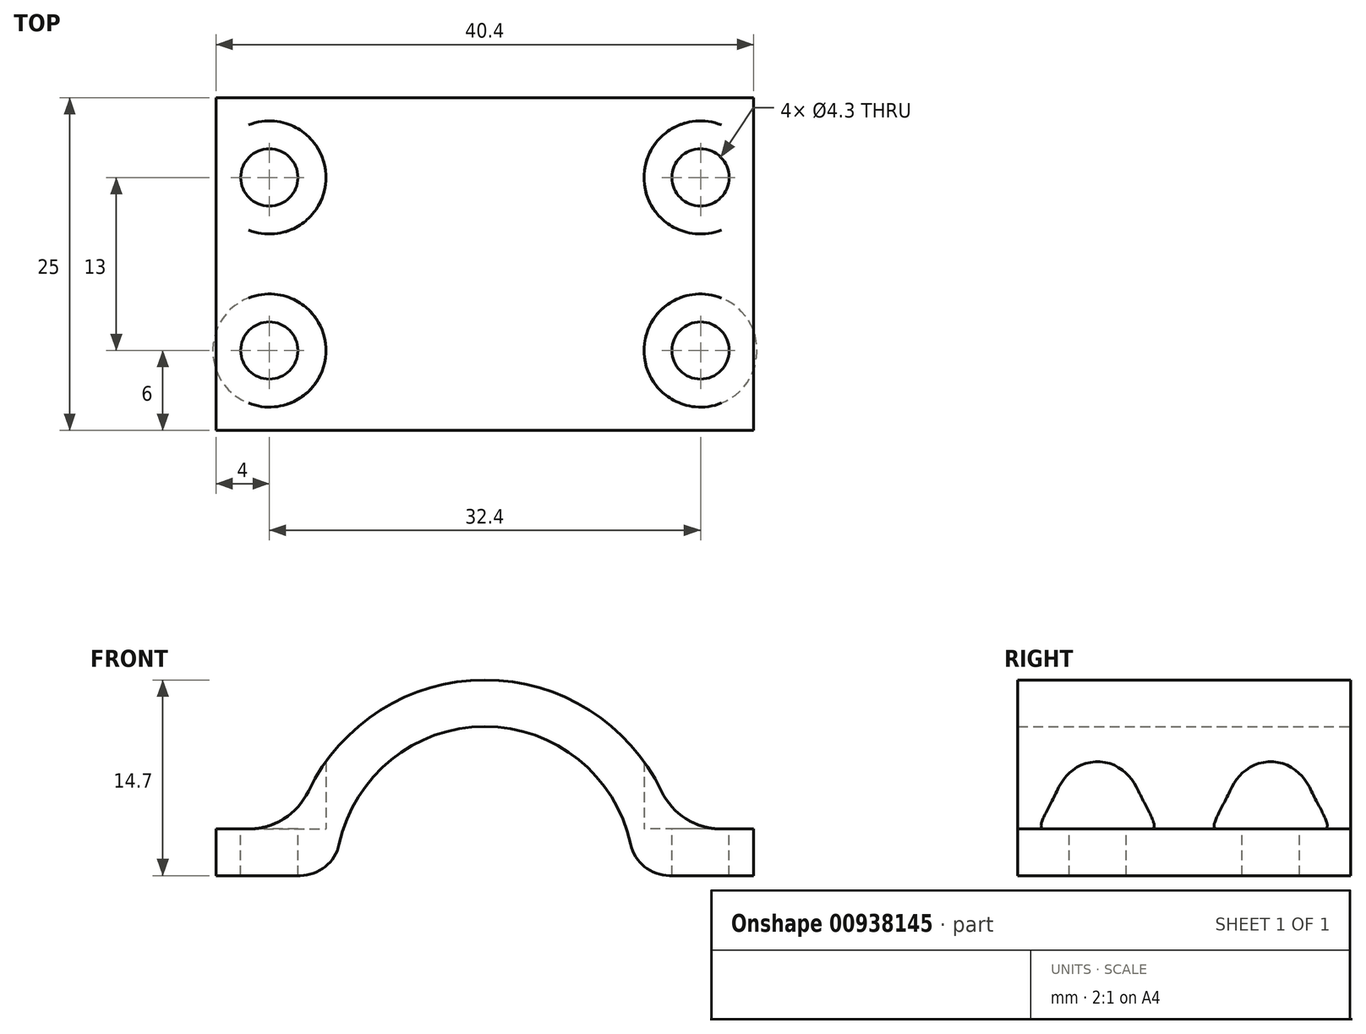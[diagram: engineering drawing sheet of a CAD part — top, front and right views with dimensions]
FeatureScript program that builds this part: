
annotation { "Feature Type Name" : "Feature", "Feature Type Description" : "" }
export const myFeature = defineFeature(function(context is Context, id is Id, definition is map)
    precondition{}
    {
        {
            var Q0;
            Q0=qCreatedBy(makeId("Front.planeOp"),FACE);
            var sketch = newSketch(context, id + "F0", { "sketchPlane" : qUnion([Q0])});
            skLineSegment(sketch, "E0", {"start": v(-13.88, 0) * mm, "end": v(-20.2, 0) * mm});
            skLineSegment(sketch, "E1", {"start": v(-20.2, 0) * mm, "end": v(-20.2, 3.5) * mm});
            skLineSegment(sketch, "E2", {"start": v(-20.2, 3.5) * mm, "end": v(-14.28, 3.5) * mm});
            skArc(sketch, "E3", {"start": v(-10.95, 2.37) * mm, "mid": v(0, 11.2) * mm, "end": v(10.95, 2.37) * mm});
            skArc(sketch, "E4", {"start": v(-14.28, 3.5) * mm, "mid": v(0, 14.7) * mm, "end": v(14.28, 3.5) * mm});
            skLineSegment(sketch, "E5", {"start": v(13.88, 0) * mm, "end": v(20.2, 0) * mm});
            skLineSegment(sketch, "E6", {"start": v(20.2, 0) * mm, "end": v(20.2, 3.5) * mm});
            skLineSegment(sketch, "E7", {"start": v(20.2, 3.5) * mm, "end": v(14.28, 3.5) * mm});
            skPoint(sketch, "E8.visualSharp", {"position": v(-11.2, 0) * mm});
            skArc(sketch, "E8.filletArc", {"start": v(-13.88, 0) * mm, "mid": v(-12, 0.67) * mm, "end": v(-10.95, 2.37) * mm});
            skPoint(sketch, "E9.visualSharp", {"position": v(11.2, 0) * mm});
            skArc(sketch, "E9.filletArc", {"start": v(10.95, 2.37) * mm, "mid": v(12, 0.67) * mm, "end": v(13.88, 0) * mm});
            skSolve(sketch);
        }
        {
            var Q0;
            Q0=makeQuery(id+"F0.imprint","IMPRINT",FACE,{"disambiguationData":[TD([[makeQuery(id+"F0.imprint","IMPRINT",EDGE,{"derivedFrom":sQuery(id+"F0.wireOp",EDGE,"E0")}),-1.0]])]});
            extrude(context, id + "F1", {"entities" : qUnion([Q0]), "depth" : 25 * mm, "offsetDistance" : 25 * mm});
        }
        {
            var Q0;
            Q0=makeQuery(id+"F1.opExtrude","SWEPT_FACE",FACE,{"disambiguationData":[OSD([sQuery(id+"F0.wireOp",EDGE,"E2")])]});
            var sketch = newSketch(context, id + "F2", { "sketchPlane" : qUnion([Q0])});
            skCircle(sketch, "E10", {"center": v(-16.2, -6) * mm, "radius": 2.15 * mm});
            skCircle(sketch, "E11", {"center": v(-16.2, -19) * mm, "radius": 2.15 * mm});
            skLineSegment(sketch, "E12", {"start": v(0, -12.5) * mm, "end": v(-26.72, -12.5) * mm, "construction": true});
            skCircle(sketch, "E13", {"center": v(16.2, -6) * mm, "radius": 2.15 * mm});
            skCircle(sketch, "E14", {"center": v(16.2, -19) * mm, "radius": 2.15 * mm});
            skCircle(sketch, "E15", {"center": v(-16.2, -6) * mm, "radius": 4.25 * mm});
            skCircle(sketch, "E16", {"center": v(16.2, -6) * mm, "radius": 4.25 * mm});
            skCircle(sketch, "E17", {"center": v(16.2, -19) * mm, "radius": 4.25 * mm});
            skCircle(sketch, "E18", {"center": v(-16.2, -19) * mm, "radius": 4.25 * mm});
            skSolve(sketch);
        }
        {
            var Q0;
            {var subQ0=sQuery(id+"F0.wireOp",EDGE,"E7");var subQ1=makeQuery(id+"F1.opExtrude","SWEPT_FACE",FACE,{"disambiguationData":[OSD([subQ0])]});var subQ2=sQuery(id+"F0.wireOp",EDGE,"E4");var subQ3=makeQuery(id+"F1.opExtrude","SWEPT_FACE",FACE,{"disambiguationData":[OSD([subQ2])]});var subQ4=sQuery(id+"F2.wireOp",EDGE,"E14");Q0=makeQuery(id+"F4.boolean.opBoolean","SPLIT",EDGE,{"disambiguationData":[topologyDisambiguationEdgeConnected([subQ3,subQ1]),TD([makeQuery(id+"F1.opExtrude","CAP_FACE",FACE,{"disambiguationData":[OSD([sQuery(id+"F0.wireOp",EDGE,"E0"),sQuery(id+"F0.wireOp",EDGE,"E1"),sQuery(id+"F0.wireOp",EDGE,"E2"),sQuery(id+"F0.wireOp",EDGE,"E3"),subQ2,sQuery(id+"F0.wireOp",EDGE,"E5"),sQuery(id+"F0.wireOp",EDGE,"E6"),subQ0,sQuery(id+"F0.wireOp",EDGE,"E8.filletArc"),sQuery(id+"F0.wireOp",EDGE,"E9.filletArc")])],"isStart":false}),subQ3,subQ1,makeQuery(id+"F4.opExtrude","SWEPT_FACE",FACE,{"disambiguationData":[OSD([subQ4])]}),makeQuery(id+"F4.opExtrude","CAP_FACE",FACE,{"disambiguationData":[OSD([subQ4])],"isStart":true})])],"derivedFrom":makeQuery(id+"F1.opExtrude","SWEPT_EDGE",EDGE,{"disambiguationData":[OSD([subQ2,subQ0])]})});}
            var Q1;
            {var subQ0=sQuery(id+"F2.wireOp",EDGE,"E13");var subQ1=sQuery(id+"F0.wireOp",EDGE,"E7");var subQ2=makeQuery(id+"F1.opExtrude","SWEPT_FACE",FACE,{"disambiguationData":[OSD([subQ1])]});var subQ3=sQuery(id+"F0.wireOp",EDGE,"E4");var subQ4=makeQuery(id+"F1.opExtrude","SWEPT_FACE",FACE,{"disambiguationData":[OSD([subQ3])]});var subQ5=sQuery(id+"F2.wireOp",EDGE,"E14");Q1=makeQuery(id+"F4.boolean.opBoolean","SPLIT",EDGE,{"disambiguationData":[topologyDisambiguationEdgeConnected([subQ4,subQ2]),TD([subQ4,subQ2,makeQuery(id+"F4.opExtrude","SWEPT_FACE",FACE,{"disambiguationData":[OSD([subQ0])]}),makeQuery(id+"F4.opExtrude","CAP_FACE",FACE,{"disambiguationData":[OSD([subQ0])],"isStart":true}),makeQuery(id+"F4.opExtrude","SWEPT_FACE",FACE,{"disambiguationData":[OSD([subQ5])]}),makeQuery(id+"F4.opExtrude","CAP_FACE",FACE,{"disambiguationData":[OSD([subQ5])],"isStart":true})])],"derivedFrom":makeQuery(id+"F1.opExtrude","SWEPT_EDGE",EDGE,{"disambiguationData":[OSD([subQ3,subQ1])]})});}
            var Q2;
            {var subQ0=sQuery(id+"F2.wireOp",EDGE,"E13");var subQ1=sQuery(id+"F0.wireOp",EDGE,"E7");var subQ2=makeQuery(id+"F1.opExtrude","SWEPT_FACE",FACE,{"disambiguationData":[OSD([subQ1])]});var subQ3=sQuery(id+"F0.wireOp",EDGE,"E4");var subQ4=makeQuery(id+"F1.opExtrude","SWEPT_FACE",FACE,{"disambiguationData":[OSD([subQ3])]});Q2=makeQuery(id+"F4.boolean.opBoolean","SPLIT",EDGE,{"disambiguationData":[topologyDisambiguationEdgeConnected([subQ4,subQ2]),TD([makeQuery(id+"F1.opExtrude","CAP_FACE",FACE,{"disambiguationData":[OSD([sQuery(id+"F0.wireOp",EDGE,"E0"),sQuery(id+"F0.wireOp",EDGE,"E1"),sQuery(id+"F0.wireOp",EDGE,"E2"),sQuery(id+"F0.wireOp",EDGE,"E3"),subQ3,sQuery(id+"F0.wireOp",EDGE,"E5"),sQuery(id+"F0.wireOp",EDGE,"E6"),subQ1,sQuery(id+"F0.wireOp",EDGE,"E8.filletArc"),sQuery(id+"F0.wireOp",EDGE,"E9.filletArc")])],"isStart":true}),subQ4,subQ2,makeQuery(id+"F4.opExtrude","SWEPT_FACE",FACE,{"disambiguationData":[OSD([subQ0])]}),makeQuery(id+"F4.opExtrude","CAP_FACE",FACE,{"disambiguationData":[OSD([subQ0])],"isStart":true})])],"derivedFrom":makeQuery(id+"F1.opExtrude","SWEPT_EDGE",EDGE,{"disambiguationData":[OSD([subQ3,subQ1])]})});}
            var Q3;
            {var subQ0=sQuery(id+"F2.wireOp",EDGE,"E11");var subQ1=sQuery(id+"F0.wireOp",EDGE,"E2");var subQ2=makeQuery(id+"F1.opExtrude","SWEPT_FACE",FACE,{"disambiguationData":[OSD([subQ1])]});var subQ3=sQuery(id+"F0.wireOp",EDGE,"E4");var subQ4=makeQuery(id+"F1.opExtrude","SWEPT_FACE",FACE,{"disambiguationData":[OSD([subQ3])]});Q3=makeQuery(id+"F4.boolean.opBoolean","SPLIT",EDGE,{"disambiguationData":[topologyDisambiguationEdgeConnected([subQ2,subQ4]),TD([makeQuery(id+"F1.opExtrude","CAP_FACE",FACE,{"disambiguationData":[OSD([sQuery(id+"F0.wireOp",EDGE,"E0"),sQuery(id+"F0.wireOp",EDGE,"E1"),subQ1,sQuery(id+"F0.wireOp",EDGE,"E3"),subQ3,sQuery(id+"F0.wireOp",EDGE,"E5"),sQuery(id+"F0.wireOp",EDGE,"E6"),sQuery(id+"F0.wireOp",EDGE,"E7"),sQuery(id+"F0.wireOp",EDGE,"E8.filletArc"),sQuery(id+"F0.wireOp",EDGE,"E9.filletArc")])],"isStart":false}),subQ2,subQ4,makeQuery(id+"F4.opExtrude","SWEPT_FACE",FACE,{"disambiguationData":[OSD([subQ0])]}),makeQuery(id+"F4.opExtrude","CAP_FACE",FACE,{"disambiguationData":[OSD([subQ0])],"isStart":true})])],"derivedFrom":makeQuery(id+"F1.opExtrude","SWEPT_EDGE",EDGE,{"disambiguationData":[OSD([subQ1,subQ3])]})});}
            var Q4;
            {var subQ0=sQuery(id+"F2.wireOp",EDGE,"E10");var subQ1=sQuery(id+"F0.wireOp",EDGE,"E4");var subQ2=makeQuery(id+"F1.opExtrude","SWEPT_FACE",FACE,{"disambiguationData":[OSD([subQ1])]});var subQ3=sQuery(id+"F0.wireOp",EDGE,"E2");var subQ4=makeQuery(id+"F1.opExtrude","SWEPT_FACE",FACE,{"disambiguationData":[OSD([subQ3])]});var subQ5=sQuery(id+"F2.wireOp",EDGE,"E11");Q4=makeQuery(id+"F4.boolean.opBoolean","SPLIT",EDGE,{"disambiguationData":[topologyDisambiguationEdgeConnected([subQ4,subQ2]),TD([subQ4,subQ2,makeQuery(id+"F4.opExtrude","SWEPT_FACE",FACE,{"disambiguationData":[OSD([subQ0])]}),makeQuery(id+"F4.opExtrude","CAP_FACE",FACE,{"disambiguationData":[OSD([subQ0])],"isStart":true}),makeQuery(id+"F4.opExtrude","SWEPT_FACE",FACE,{"disambiguationData":[OSD([subQ5])]}),makeQuery(id+"F4.opExtrude","CAP_FACE",FACE,{"disambiguationData":[OSD([subQ5])],"isStart":true})])],"derivedFrom":makeQuery(id+"F1.opExtrude","SWEPT_EDGE",EDGE,{"disambiguationData":[OSD([subQ3,subQ1])]})});}
            var Q5;
            {var subQ0=sQuery(id+"F2.wireOp",EDGE,"E10");var subQ1=sQuery(id+"F0.wireOp",EDGE,"E4");var subQ2=sQuery(id+"F0.wireOp",EDGE,"E2");var subQ3=makeQuery(id+"F1.opExtrude","SWEPT_FACE",FACE,{"disambiguationData":[OSD([subQ2])]});var subQ4=makeQuery(id+"F1.opExtrude","SWEPT_FACE",FACE,{"disambiguationData":[OSD([subQ1])]});Q5=makeQuery(id+"F4.boolean.opBoolean","SPLIT",EDGE,{"disambiguationData":[topologyDisambiguationEdgeConnected([subQ3,subQ4]),TD([makeQuery(id+"F1.opExtrude","CAP_FACE",FACE,{"disambiguationData":[OSD([sQuery(id+"F0.wireOp",EDGE,"E0"),sQuery(id+"F0.wireOp",EDGE,"E1"),subQ2,sQuery(id+"F0.wireOp",EDGE,"E3"),subQ1,sQuery(id+"F0.wireOp",EDGE,"E5"),sQuery(id+"F0.wireOp",EDGE,"E6"),sQuery(id+"F0.wireOp",EDGE,"E7"),sQuery(id+"F0.wireOp",EDGE,"E8.filletArc"),sQuery(id+"F0.wireOp",EDGE,"E9.filletArc")])],"isStart":true}),subQ3,subQ4,makeQuery(id+"F4.opExtrude","SWEPT_FACE",FACE,{"disambiguationData":[OSD([subQ0])]}),makeQuery(id+"F4.opExtrude","CAP_FACE",FACE,{"disambiguationData":[OSD([subQ0])],"isStart":true})])],"derivedFrom":makeQuery(id+"F1.opExtrude","SWEPT_EDGE",EDGE,{"disambiguationData":[OSD([subQ2,subQ1])]})});}
            fillet(context, id + "F3", {"entities" : qUnion([Q0, Q1, Q2, Q3, Q4, Q5]), "tangentPropagation" : true, "radius" : 5 * mm, "defaultsChanged" : false, "vertexSettings" : [], "allowEdgeOverflow" : false});
        }
        {
            var Q0;
            {var subQ0=sQuery(id+"F2.wireOp",EDGE,"E10");var subQ1=makeQuery(id+"F1.opExtrude","SWEPT_EDGE",EDGE,{"disambiguationData":[OSD([sQuery(id+"F0.wireOp",EDGE,"E2"),sQuery(id+"F0.wireOp",EDGE,"E4")])]});var subQ2=makeQuery(id+"F2.imprint","INTERSECT",VERTEX,{"disambiguationData":[OD(0.0)],"derivedFrom":[subQ1,subQ0]});Q0=makeQuery(id+"F2.imprint","IMPRINT",FACE,{"disambiguationData":[TD([[makeQuery(id+"F2.imprint","IMPRINT",EDGE,{"disambiguationData":[TD([[subQ2,1.0]])],"derivedFrom":subQ0}),1.0]])]});}
            var Q1;
            {var subQ0=sQuery(id+"F2.wireOp",EDGE,"E10");var subQ1=makeQuery(id+"F1.opExtrude","SWEPT_EDGE",EDGE,{"disambiguationData":[OSD([sQuery(id+"F0.wireOp",EDGE,"E2"),sQuery(id+"F0.wireOp",EDGE,"E4")])]});var subQ2=makeQuery(id+"F2.imprint","INTERSECT",VERTEX,{"disambiguationData":[OD(0.0)],"derivedFrom":[subQ1,subQ0]});Q1=makeQuery(id+"F2.imprint","IMPRINT",FACE,{"disambiguationData":[TD([[makeQuery(id+"F2.imprint","IMPRINT",EDGE,{"disambiguationData":[TD([[subQ2,-1.0]])],"derivedFrom":subQ0}),1.0]])]});}
            var Q2;
            {var subQ0=sQuery(id+"F2.wireOp",EDGE,"E11");var subQ1=makeQuery(id+"F1.opExtrude","SWEPT_EDGE",EDGE,{"disambiguationData":[OSD([sQuery(id+"F0.wireOp",EDGE,"E2"),sQuery(id+"F0.wireOp",EDGE,"E4")])]});var subQ2=makeQuery(id+"F2.imprint","INTERSECT",VERTEX,{"disambiguationData":[OD(0.0)],"derivedFrom":[subQ1,subQ0]});Q2=makeQuery(id+"F2.imprint","IMPRINT",FACE,{"disambiguationData":[TD([[makeQuery(id+"F2.imprint","IMPRINT",EDGE,{"disambiguationData":[TD([[subQ2,-1.0]])],"derivedFrom":subQ0}),1.0]])]});}
            var Q3;
            {var subQ0=sQuery(id+"F2.wireOp",EDGE,"E11");var subQ1=makeQuery(id+"F1.opExtrude","SWEPT_EDGE",EDGE,{"disambiguationData":[OSD([sQuery(id+"F0.wireOp",EDGE,"E2"),sQuery(id+"F0.wireOp",EDGE,"E4")])]});var subQ2=makeQuery(id+"F2.imprint","INTERSECT",VERTEX,{"disambiguationData":[OD(0.0)],"derivedFrom":[subQ1,subQ0]});Q3=makeQuery(id+"F2.imprint","IMPRINT",FACE,{"disambiguationData":[TD([[makeQuery(id+"F2.imprint","IMPRINT",EDGE,{"disambiguationData":[TD([[subQ2,1.0]])],"derivedFrom":subQ0}),1.0]])]});}
            var Q4;
            Q4=makeQuery(id+"F2.imprint","IMPRINT",FACE,{"disambiguationData":[TD([[makeQuery(id+"F2.imprint","IMPRINT",EDGE,{"derivedFrom":sQuery(id+"F2.wireOp",EDGE,"E14")}),1.0]])]});
            var Q5;
            Q5=makeQuery(id+"F2.imprint","IMPRINT",FACE,{"disambiguationData":[TD([[makeQuery(id+"F2.imprint","IMPRINT",EDGE,{"derivedFrom":sQuery(id+"F2.wireOp",EDGE,"E13")}),1.0]])]});
            extrude(context, id + "F4", {"entities" : qUnion([Q0, Q1, Q2, Q3, Q4, Q5]), "operationType" : NewBodyOperationType.REMOVE, "endBound" : BoundingType.THROUGH_ALL, "oppositeDirection" : true, "depth" : 25 * mm, "offsetDistance" : 25 * mm});
        }
        {
            var Q0;
            {var subQ1=sQuery(id+"F0.wireOp",EDGE,"E2");var subQ5=makeQuery(id+"F1.opExtrude","SWEPT_EDGE",EDGE,{"disambiguationData":[OSD([subQ1,sQuery(id+"F0.wireOp",EDGE,"E4")])]});var subQ8=sQuery(id+"F2.wireOp",EDGE,"E10");var subQ9=makeQuery(id+"F2.imprint","INTERSECT",VERTEX,{"disambiguationData":[OD(0.0)],"derivedFrom":[subQ5,subQ8]});Q0=makeQuery(id+"F2.imprint","IMPRINT",FACE,{"disambiguationData":[TD([[makeQuery(id+"F2.imprint","IMPRINT",EDGE,{"disambiguationData":[TD([[subQ9,-1.0]])],"derivedFrom":subQ8}),-1.0]])]});}
            var Q1;
            {var subQ0=sQuery(id+"F2.wireOp",EDGE,"E10");var subQ1=makeQuery(id+"F1.opExtrude","SWEPT_EDGE",EDGE,{"disambiguationData":[OSD([sQuery(id+"F0.wireOp",EDGE,"E2"),sQuery(id+"F0.wireOp",EDGE,"E4")])]});var subQ2=makeQuery(id+"F2.imprint","INTERSECT",VERTEX,{"disambiguationData":[OD(0.0)],"derivedFrom":[subQ1,subQ0]});Q1=makeQuery(id+"F2.imprint","IMPRINT",FACE,{"disambiguationData":[TD([[makeQuery(id+"F2.imprint","IMPRINT",EDGE,{"disambiguationData":[TD([[subQ2,1.0]])],"derivedFrom":subQ0}),-1.0]])]});}
            var Q2;
            {var subQ1=sQuery(id+"F0.wireOp",EDGE,"E2");var subQ5=makeQuery(id+"F1.opExtrude","SWEPT_EDGE",EDGE,{"disambiguationData":[OSD([subQ1,sQuery(id+"F0.wireOp",EDGE,"E4")])]});var subQ8=sQuery(id+"F2.wireOp",EDGE,"E11");var subQ9=makeQuery(id+"F2.imprint","INTERSECT",VERTEX,{"disambiguationData":[OD(0.0)],"derivedFrom":[subQ5,subQ8]});Q2=makeQuery(id+"F2.imprint","IMPRINT",FACE,{"disambiguationData":[TD([[makeQuery(id+"F2.imprint","IMPRINT",EDGE,{"disambiguationData":[TD([[subQ9,-1.0]])],"derivedFrom":subQ8}),-1.0]])]});}
            var Q3;
            {var subQ0=sQuery(id+"F2.wireOp",EDGE,"E11");var subQ1=makeQuery(id+"F1.opExtrude","SWEPT_EDGE",EDGE,{"disambiguationData":[OSD([sQuery(id+"F0.wireOp",EDGE,"E2"),sQuery(id+"F0.wireOp",EDGE,"E4")])]});var subQ2=makeQuery(id+"F2.imprint","INTERSECT",VERTEX,{"disambiguationData":[OD(0.0)],"derivedFrom":[subQ1,subQ0]});Q3=makeQuery(id+"F2.imprint","IMPRINT",FACE,{"disambiguationData":[TD([[makeQuery(id+"F2.imprint","IMPRINT",EDGE,{"disambiguationData":[TD([[subQ2,1.0]])],"derivedFrom":subQ0}),-1.0]])]});}
            var Q4;
            Q4=makeQuery(id+"F2.imprint","IMPRINT",FACE,{"disambiguationData":[TD([[makeQuery(id+"F2.imprint","IMPRINT",EDGE,{"derivedFrom":sQuery(id+"F2.wireOp",EDGE,"E14")}),-1.0]])]});
            var Q5;
            Q5=makeQuery(id+"F2.imprint","IMPRINT",FACE,{"disambiguationData":[TD([[makeQuery(id+"F2.imprint","IMPRINT",EDGE,{"derivedFrom":sQuery(id+"F2.wireOp",EDGE,"E14")}),1.0]])]});
            var Q6;
            Q6=makeQuery(id+"F2.imprint","IMPRINT",FACE,{"disambiguationData":[TD([[makeQuery(id+"F2.imprint","IMPRINT",EDGE,{"derivedFrom":sQuery(id+"F2.wireOp",EDGE,"E13")}),-1.0]])]});
            var Q7;
            Q7=makeQuery(id+"F2.imprint","IMPRINT",FACE,{"disambiguationData":[TD([[makeQuery(id+"F2.imprint","IMPRINT",EDGE,{"derivedFrom":sQuery(id+"F2.wireOp",EDGE,"E13")}),1.0]])]});
            var Q8;
            {var subQ0=sQuery(id+"F2.wireOp",EDGE,"E10");var subQ1=makeQuery(id+"F1.opExtrude","SWEPT_EDGE",EDGE,{"disambiguationData":[OSD([sQuery(id+"F0.wireOp",EDGE,"E2"),sQuery(id+"F0.wireOp",EDGE,"E4")])]});var subQ2=makeQuery(id+"F2.imprint","INTERSECT",VERTEX,{"disambiguationData":[OD(0.0)],"derivedFrom":[subQ1,subQ0]});Q8=makeQuery(id+"F2.imprint","IMPRINT",FACE,{"disambiguationData":[TD([[makeQuery(id+"F2.imprint","IMPRINT",EDGE,{"disambiguationData":[TD([[subQ2,1.0]])],"derivedFrom":subQ0}),1.0]])]});}
            var Q9;
            {var subQ0=sQuery(id+"F2.wireOp",EDGE,"E11");var subQ1=makeQuery(id+"F1.opExtrude","SWEPT_EDGE",EDGE,{"disambiguationData":[OSD([sQuery(id+"F0.wireOp",EDGE,"E2"),sQuery(id+"F0.wireOp",EDGE,"E4")])]});var subQ2=makeQuery(id+"F2.imprint","INTERSECT",VERTEX,{"disambiguationData":[OD(0.0)],"derivedFrom":[subQ1,subQ0]});Q9=makeQuery(id+"F2.imprint","IMPRINT",FACE,{"disambiguationData":[TD([[makeQuery(id+"F2.imprint","IMPRINT",EDGE,{"disambiguationData":[TD([[subQ2,1.0]])],"derivedFrom":subQ0}),1.0]])]});}
            var Q10;
            Q10=makeQuery(id+"F4.boolean.opBoolean","COPY",FACE,{"derivedFrom":makeQuery(id+"F4.opExtrude","CAP_FACE",FACE,{"disambiguationData":[OSD([sQuery(id+"F2.wireOp",EDGE,"E11")])],"isStart":true})});
            var Q11;
            {var subQ0=sQuery(id+"F2.wireOp",EDGE,"E10");var subQ1=makeQuery(id+"F1.opExtrude","SWEPT_EDGE",EDGE,{"disambiguationData":[OSD([sQuery(id+"F0.wireOp",EDGE,"E2"),sQuery(id+"F0.wireOp",EDGE,"E4")])]});var subQ2=makeQuery(id+"F2.imprint","INTERSECT",VERTEX,{"disambiguationData":[OD(0.0)],"derivedFrom":[subQ1,subQ0]});Q11=makeQuery(id+"F2.imprint","IMPRINT",FACE,{"disambiguationData":[TD([[makeQuery(id+"F2.imprint","IMPRINT",EDGE,{"disambiguationData":[TD([[subQ2,-1.0]])],"derivedFrom":subQ0}),1.0]])]});}
            var Q12;
            Q12=makeQuery(id+"F4.boolean.opBoolean","COPY",FACE,{"derivedFrom":makeQuery(id+"F4.opExtrude","CAP_FACE",FACE,{"disambiguationData":[OSD([sQuery(id+"F2.wireOp",EDGE,"E10")])],"isStart":true})});
            extrude(context, id + "F5", {"entities" : qUnion([Q0, Q1, Q2, Q3, Q4, Q5, Q6, Q7, Q8, Q9, Q10, Q11, Q12]), "operationType" : NewBodyOperationType.REMOVE, "endBound" : BoundingType.THROUGH_ALL, "depth" : 25 * mm, "offsetDistance" : 25 * mm});
        }
    });
